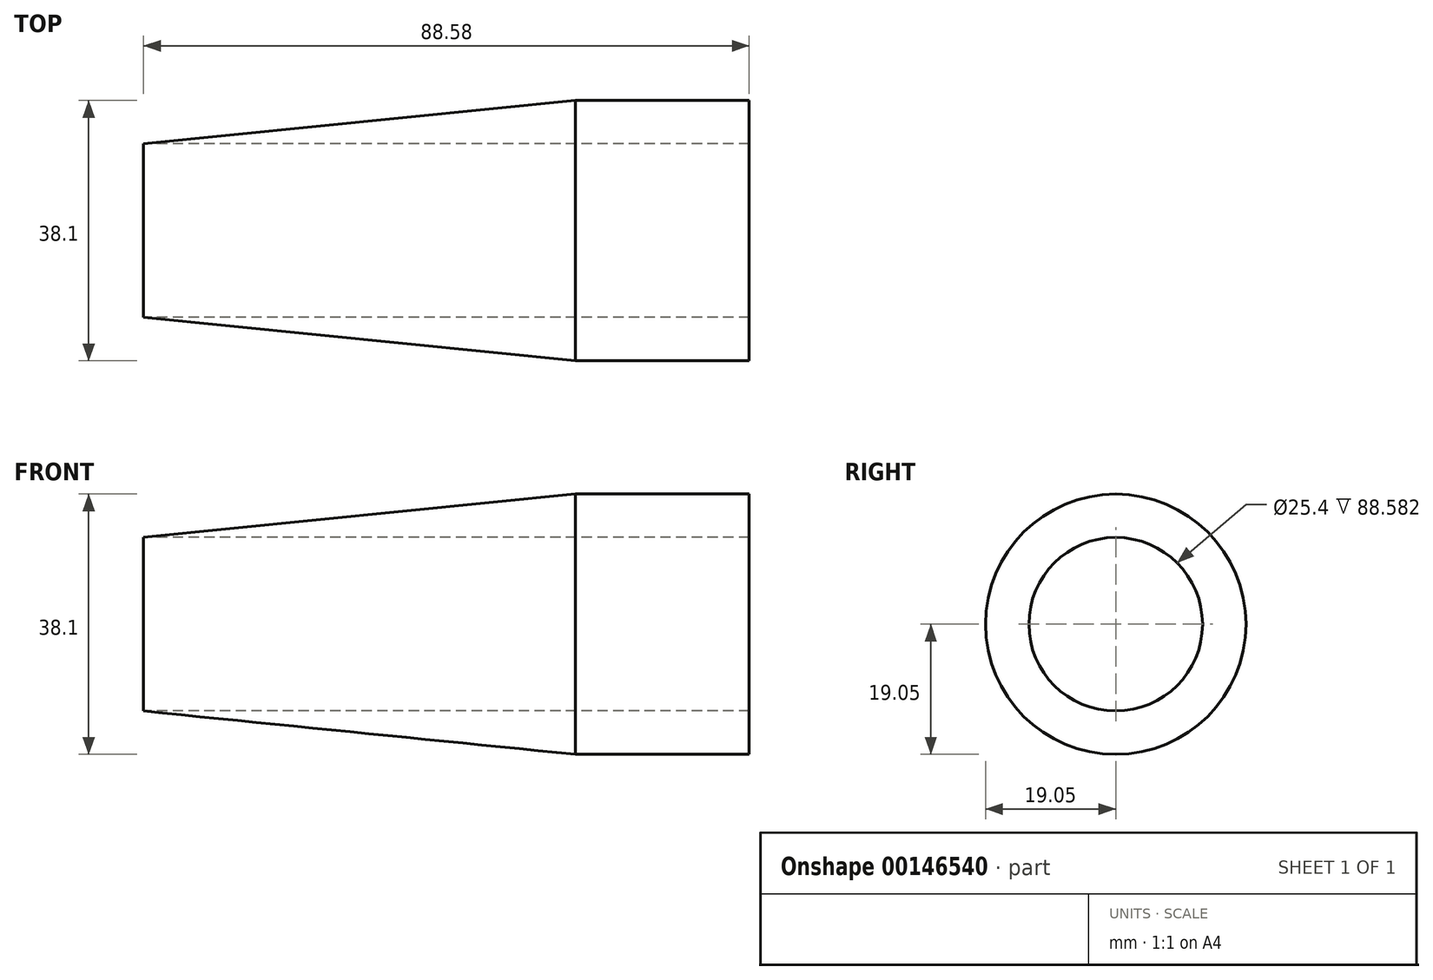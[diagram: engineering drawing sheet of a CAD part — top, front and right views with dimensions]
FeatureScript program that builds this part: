
annotation { "Feature Type Name" : "Feature", "Feature Type Description" : "" }
export const myFeature = defineFeature(function(context is Context, id is Id, definition is map)
    precondition{}
    {
        {
            var Q0;
            Q0=qCreatedBy(makeId("Front.planeOp"),FACE);
            var sketch = newSketch(context, id + "F0", { "sketchPlane" : qUnion([Q0])});
            skLineSegment(sketch, "E0", {"start": v(0, 0) * mm, "end": v(0, 12.7) * mm});
            skLineSegment(sketch, "E1", {"start": v(0, 12.7) * mm, "end": v(63.18, 19.05) * mm});
            skLineSegment(sketch, "E2", {"start": v(63.18, 19.05) * mm, "end": v(63.18, 0) * mm});
            skLineSegment(sketch, "E3", {"start": v(63.18, 0) * mm, "end": v(0, 0) * mm});
            skSolve(sketch);
        }
        {
            var Q0;
            Q0 = qSketchRegion(id + "F0", true);
            var Q1;
            Q1=sQuery(id+"F0.wireOp",EDGE,"E3");
            revolve(context, id + "F1", {"entities" : qUnion([Q0]), "axis" : qUnion([Q1]), "revolveType" : RevolveType.FULL});
        }
        {
            var Q0;
            Q0=makeQuery(id+"F1.opRevolve","SWEPT_FACE",FACE,{"disambiguationData":[OSD([sQuery(id+"F0.wireOp",EDGE,"E2")])]});
            var sketch = newSketch(context, id + "F2", { "sketchPlane" : qUnion([Q0])});
            skCircle(sketch, "E4", {"center": v(0, 0) * mm, "radius": 19.05 * mm});
            skSolve(sketch);
        }
        {
            var Q0;
            Q0 = qSketchRegion(id + "F2", true);
            extrude(context, id + "F3", {"entities" : qUnion([Q0]), "operationType" : NewBodyOperationType.ADD, "depth" : 25.4 * mm});
        }
        {
            var Q0;
            Q0=makeQuery(id+"F3.opExtrude","CAP_FACE",FACE,{"disambiguationData":[OSD([sQuery(id+"F2.wireOp",EDGE,"E4")])],"isStart":false});
            shell(context, id + "F4", {"entities" : qUnion([Q0]), "thickness" : 6.35 * mm});
        }
        {
            var Q0;
            Q0=makeQuery(id+"F4.opShell","OFFSET_FACE",FACE,{"disambiguationData":[OSD([sQuery(id+"F0.wireOp",EDGE,"E0")])]});
            var sketch = newSketch(context, id + "F5", { "sketchPlane" : qUnion([Q0])});
            skPoint(sketch, "E5", {"position": v(0, 0) * mm});
            skSolve(sketch);
        }
        {
            var Q0;
            Q0=sQuery(id+"F5.wireOp",VERTEX,"E5");
            var Q1;
            Q1=makeQuery(id+"F1.opRevolve","SWEPT_BODY",BODY,{"disambiguationData":[OSD([sQuery(id+"F0.wireOp",EDGE,"E0"),sQuery(id+"F0.wireOp",EDGE,"E1"),sQuery(id+"F0.wireOp",EDGE,"E2"),sQuery(id+"F0.wireOp",EDGE,"E3")])]});
            hole(context, id + "F6", {"style" : HoleStyle.SIMPLE, "endStyle" : HoleEndStyle.THROUGH, "oppositeDirection" : true, "holeDiameter" : 25.4 * mm, "locations" : qUnion([Q0]), "scope" : qUnion([Q1]), "isTappedThrough" : true});
        }
        {
            var Q0;
            Q0=makeQuery(id+"F6.hole-0.boolean.opBoolean","MERGE",FACE,{"derivedFrom":[makeQuery(id+"F4.opShell","OFFSET_FACE",FACE,{"disambiguationData":[OSD([sQuery(id+"F0.wireOp",EDGE,"E0")])]}),makeQuery(id+"F6.hole-0.opRevolve","SWEPT_FACE",FACE,{"disambiguationData":[OSD([sQuery(id+"F6.hole-0.sketch.wireOp",EDGE,"core_line_3")])]})]});
            var sketch = newSketch(context, id + "F7", { "sketchPlane" : qUnion([Q0])});
            skPoint(sketch, "E6", {"position": v(0, 0) * mm});
            skSolve(sketch);
        }
        {
            var Q0;
            Q0=sQuery(id+"F7.wireOp",VERTEX,"E6");
            var Q1;
            Q1=makeQuery(id+"F1.opRevolve","SWEPT_BODY",BODY,{"disambiguationData":[OSD([sQuery(id+"F0.wireOp",EDGE,"E0"),sQuery(id+"F0.wireOp",EDGE,"E1"),sQuery(id+"F0.wireOp",EDGE,"E2"),sQuery(id+"F0.wireOp",EDGE,"E3")])]});
            hole(context, id + "F8", {"style" : HoleStyle.SIMPLE, "endStyle" : HoleEndStyle.THROUGH, "holeDiameter" : 25.4 * mm, "locations" : qUnion([Q0]), "scope" : qUnion([Q1]), "isTappedThrough" : true});
        }
    });
